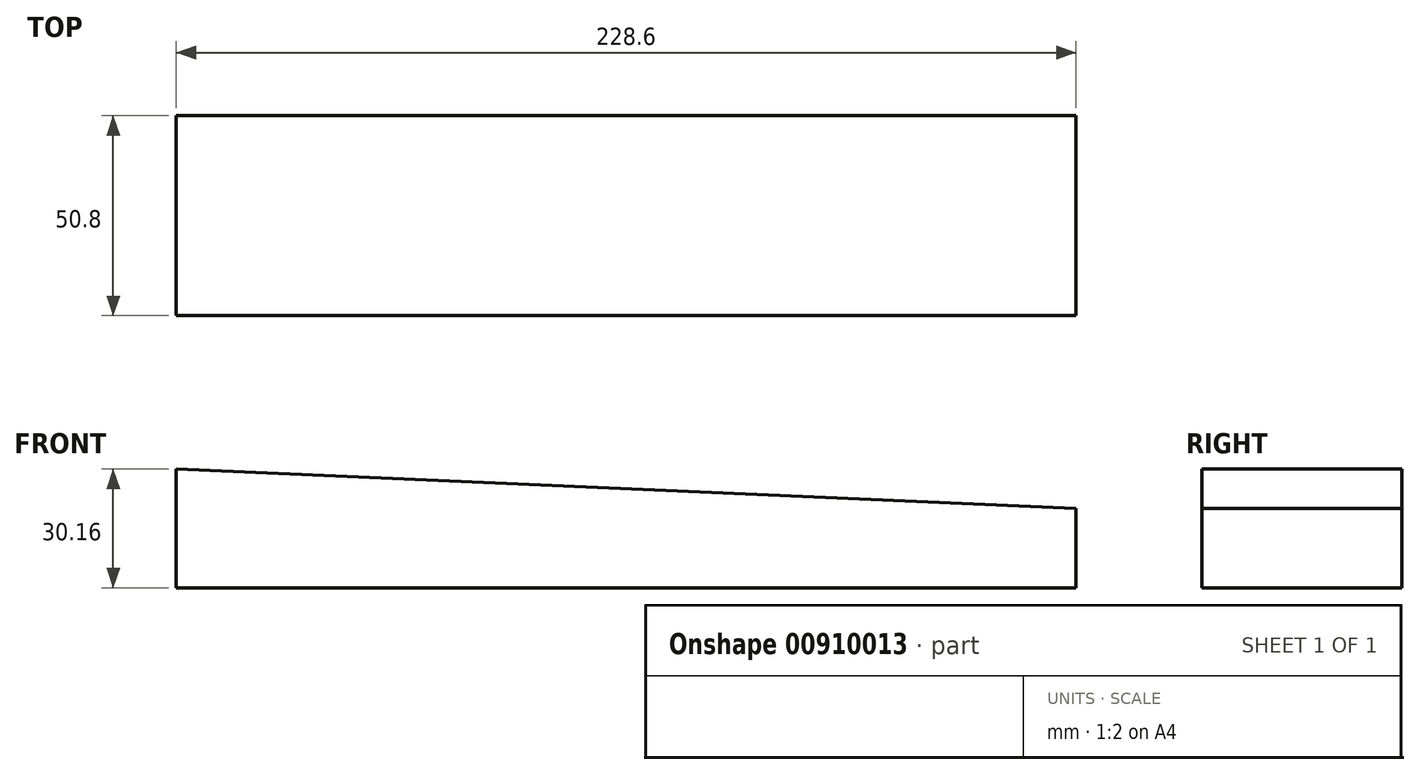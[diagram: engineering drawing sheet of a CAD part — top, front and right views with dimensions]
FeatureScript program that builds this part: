
annotation { "Feature Type Name" : "Feature", "Feature Type Description" : "" }
export const myFeature = defineFeature(function(context is Context, id is Id, definition is map)
    precondition{}
    {
        {
            var Q0;
            Q0=qCreatedBy(makeId("Front.planeOp"),FACE);
            var sketch = newSketch(context, id + "F0", { "sketchPlane" : qUnion([Q0])});
            skLineSegment(sketch, "E0", {"start": v(0, 0) * mm, "end": v(228.6, 0) * mm});
            skLineSegment(sketch, "E1", {"start": v(228.6, 0) * mm, "end": v(228.6, 20.18) * mm});
            skLineSegment(sketch, "E2", {"start": v(228.6, 20.18) * mm, "end": v(0, 30.16) * mm});
            skLineSegment(sketch, "E3", {"start": v(0, 30.16) * mm, "end": v(0, 0) * mm});
            skSolve(sketch);
        }
        {
            var Q0;
            Q0=makeQuery(id+"F0.imprint","IMPRINT",FACE,{"disambiguationData":[TD([[makeQuery(id+"F0.imprint","IMPRINT",EDGE,{"derivedFrom":sQuery(id+"F0.wireOp",EDGE,"E0")}),1.0]])]});
            extrude(context, id + "F1", {"entities" : qUnion([Q0]), "depth" : 50.8 * mm, "offsetDistance" : 25 * mm, "symmetric" : true});
        }
    });
